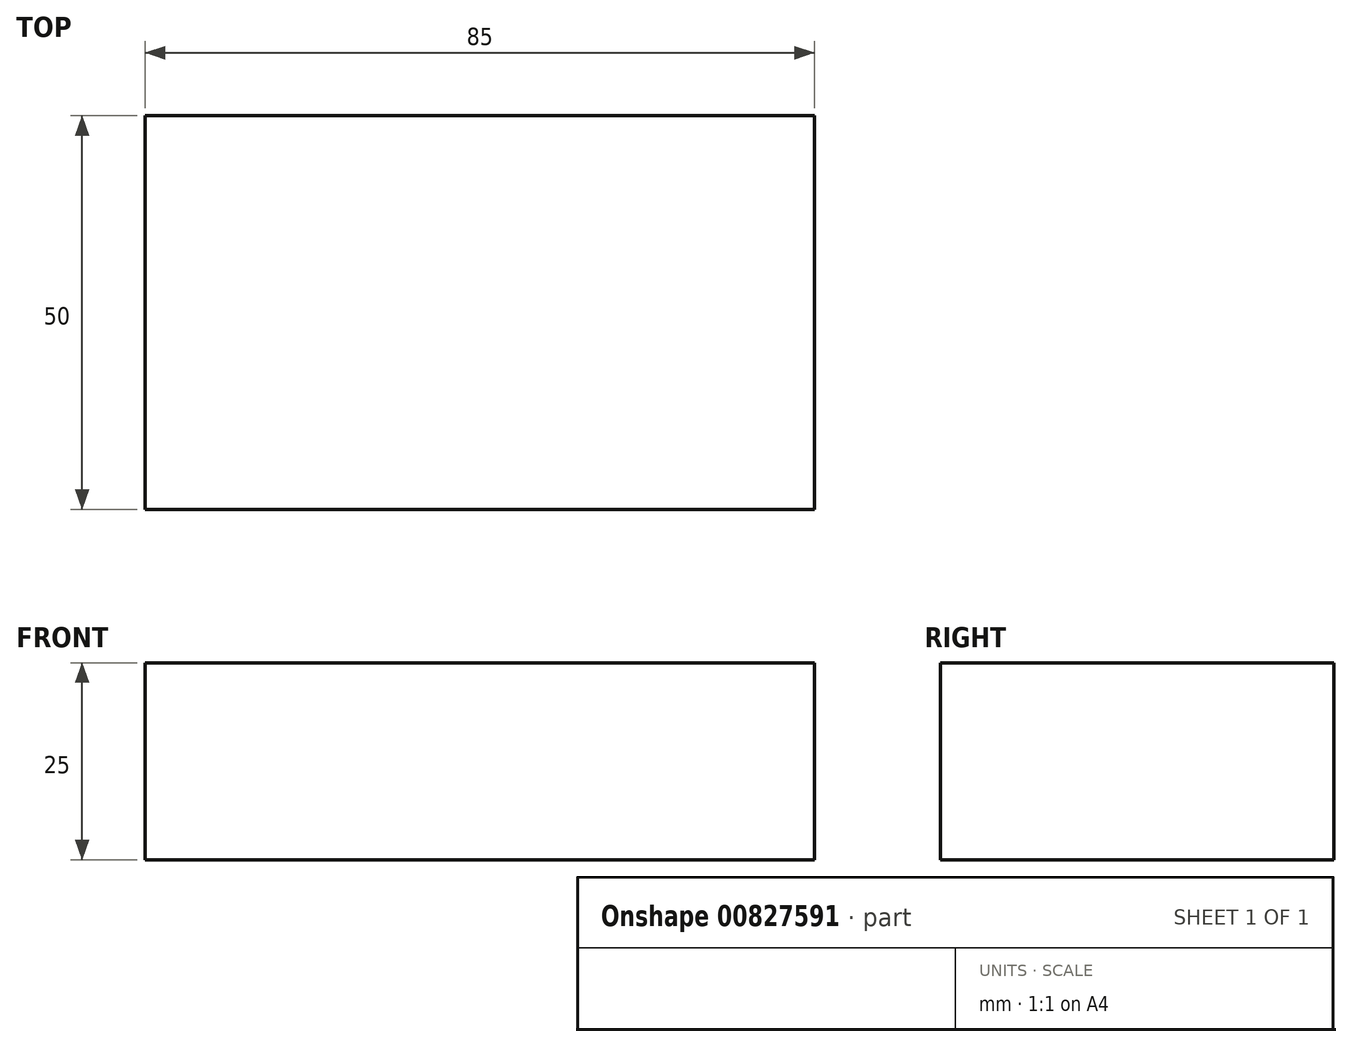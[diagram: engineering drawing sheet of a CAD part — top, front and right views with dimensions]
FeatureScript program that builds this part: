
annotation { "Feature Type Name" : "Feature", "Feature Type Description" : "" }
export const myFeature = defineFeature(function(context is Context, id is Id, definition is map)
    precondition{}
    {
        {
            var Q0;
            Q0=qCreatedBy(makeId("Top.planeOp"),FACE);
            var sketch = newSketch(context, id + "F0", { "sketchPlane" : qUnion([Q0])});
            skLineSegment(sketch, "E0.bottom", {"start": v(-42.5, 25) * mm, "end": v(42.5, 25) * mm});
            skLineSegment(sketch, "E0.top", {"start": v(-42.5, -25) * mm, "end": v(42.5, -25) * mm});
            skLineSegment(sketch, "E0.left", {"start": v(-42.5, 25) * mm, "end": v(-42.5, -25) * mm});
            skLineSegment(sketch, "E0.right", {"start": v(42.5, 25) * mm, "end": v(42.5, -25) * mm});
            skPoint(sketch, "E0.middle", {"position": v(0, 0) * mm});
            skSolve(sketch);
        }
        {
            var Q0;
            Q0 = qSketchRegion(id + "F0", true);
            extrude(context, id + "F1", {"entities" : qUnion([Q0]), "depth" : 25 * mm, "offsetDistance" : 25 * mm});
        }
    });
